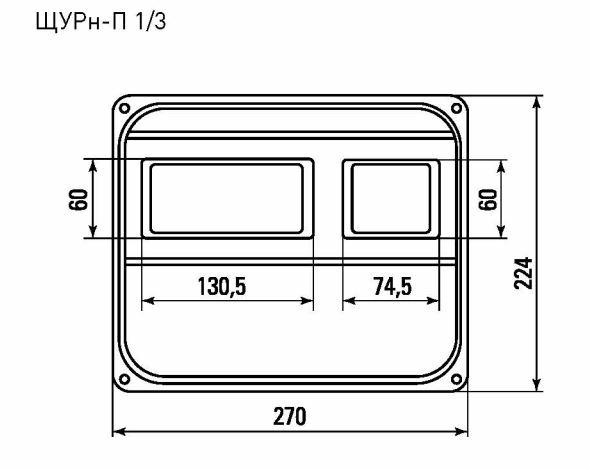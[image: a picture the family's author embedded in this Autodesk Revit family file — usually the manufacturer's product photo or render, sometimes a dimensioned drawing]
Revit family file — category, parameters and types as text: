
# Revit family: EKF_EE_Короб_КЭТ_Силовой(1890х300х150)_Basic
name_source: partatom
category: Электрооборудование
units: mm (PartAtom-declared; Revit-internal decimal feet)

## family parameters
Всегда вертикально = Да
На основе рабочей плоскости = Нет
Общий = Нет
При загрузке вырезать с полостями = Нет
Размер круглого соединителя = Использовать диаметр
Тип детали = Силовой щит
Точка расчета площади = Да

## types (1)
- Короб КЭТ силовой (1890х300х150) EKF Basic
    ADSK_Единица измерения = компл.
    ADSK_Завод-изготовитель = EKF
    ADSK_Классификация нагрузок = Прочее
    ADSK_Код изделия = uerm-ket-s-1890
    ADSK_Количество = 1
    ADSK_Количество фаз = 3
    ADSK_Коэффициент мощности = 1
    ADSK_Марка = Короб КЭТ силовой
    ADSK_Масса = 0
    ADSK_Материал = RAL 7035_Сталь
    ADSK_Наименование = Короб КЭТ силовой (1890х300х150) EKF BasicКороб КЭТ силовой (1890х300х150) EKF Basic
    ADSK_Напряжение = 400 В
    ADSK_Номинальная мощность = 0 Вт
    ADSK_Обозначение = Короб КЭТ силовой
    ADSK_Полная мощность = 0 В·А
    ADSK_Размер_Высота = 1890 мм
    ADSK_Размер_Глубина = 150 мм
    ADSK_Размер_Ширина = 300 мм
    ADSK_Ток = 125 А
    Изготовитель = EKF
    Количество DIN-реек = 0
    Количество модулей на DIN-рейке = 0
    Максимальное количество модулей = 0
    Описание = Короб КЭТ силовой (1890х300х150) EKF BasicКороб КЭТ силовой (1890х300х150) EKF Basic
    Серия номенклатуры = Basic
    Степень защиты IP = IP31
    ТВ = EKF
    Тип = 203 мм
    Тип установки = Навесной
